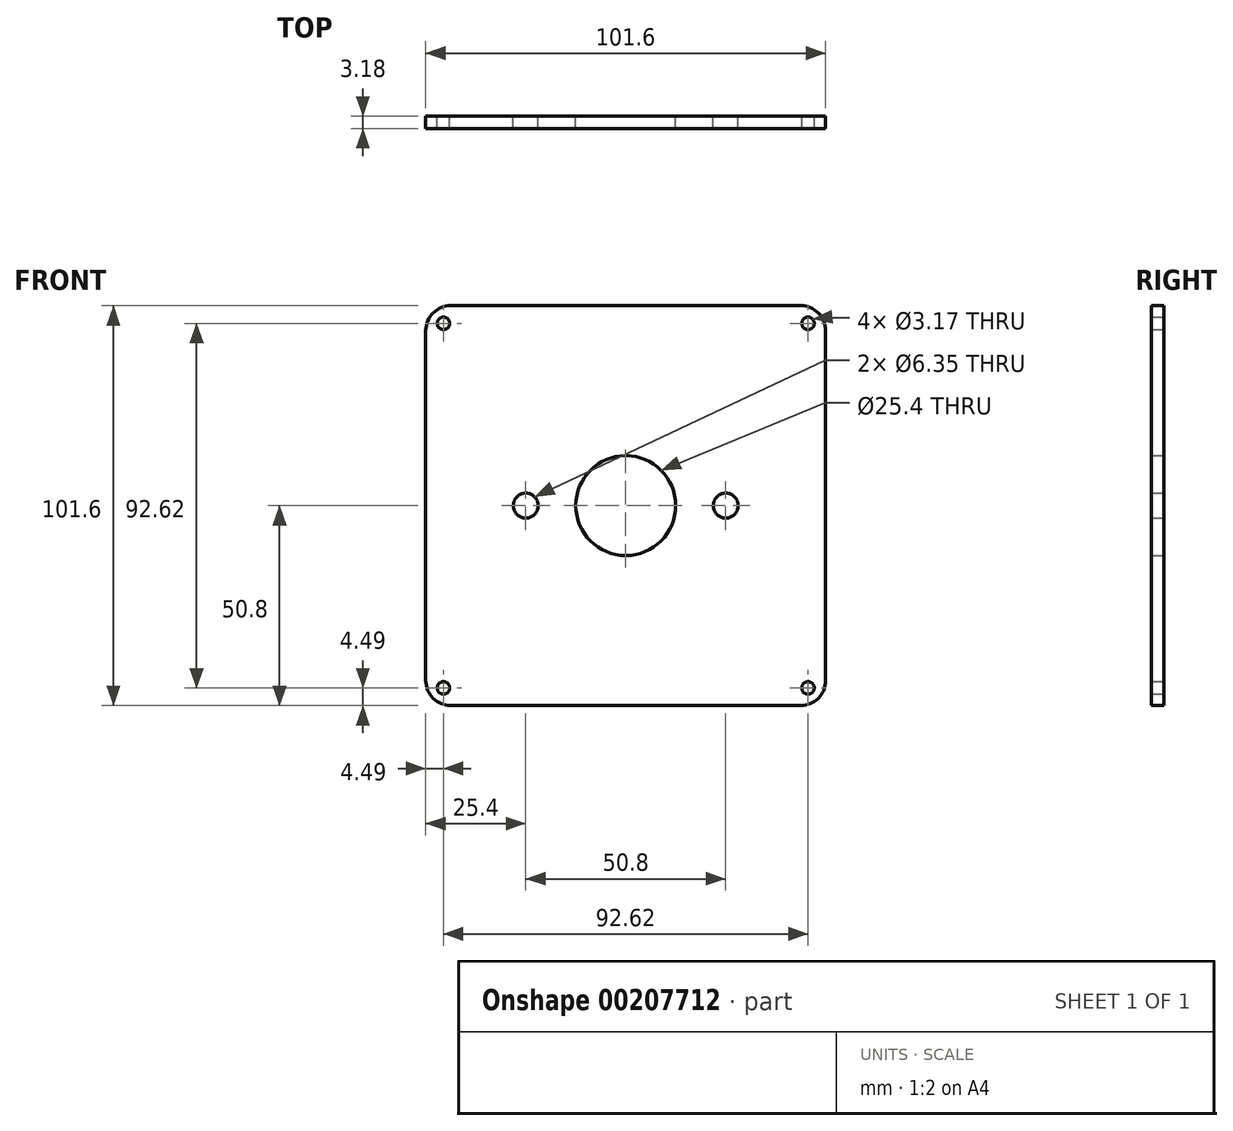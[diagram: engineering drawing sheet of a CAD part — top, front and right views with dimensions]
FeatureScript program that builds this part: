
annotation { "Feature Type Name" : "Feature", "Feature Type Description" : "" }
export const myFeature = defineFeature(function(context is Context, id is Id, definition is map)
    precondition{}
    {
        {
            var Q0;
            Q0=qCreatedBy(makeId("Front.planeOp"),FACE);
            var sketch = newSketch(context, id + "F0", { "sketchPlane" : qUnion([Q0])});
            skLineSegment(sketch, "E0.bottom", {"start": v(44.45, -50.8) * mm, "end": v(-44.45, -50.8) * mm});
            skLineSegment(sketch, "E0.top", {"start": v(44.45, 50.8) * mm, "end": v(-44.45, 50.8) * mm});
            skLineSegment(sketch, "E0.left", {"start": v(50.8, -44.45) * mm, "end": v(50.8, 44.45) * mm});
            skLineSegment(sketch, "E0.right", {"start": v(-50.8, -44.45) * mm, "end": v(-50.8, 44.45) * mm});
            skPoint(sketch, "E0.middle", {"position": v(0, 0) * mm});
            skCircle(sketch, "E1", {"center": v(0, 0) * mm, "radius": 12.7 * mm});
            skCircle(sketch, "E2", {"center": v(-25.4, 0) * mm, "radius": 3.18 * mm});
            skCircle(sketch, "E3", {"center": v(25.4, 0) * mm, "radius": 3.18 * mm});
            skCircle(sketch, "E4", {"center": v(0, 0) * mm, "radius": 25.4 * mm, "construction": true});
            skPoint(sketch, "E5.visualSharp", {"position": v(-50.8, 50.8) * mm});
            skArc(sketch, "E5.filletArc", {"start": v(-44.45, 50.8) * mm, "mid": v(-48.94, 48.94) * mm, "end": v(-50.8, 44.45) * mm});
            skPoint(sketch, "E6.visualSharp", {"position": v(-50.8, -50.8) * mm});
            skArc(sketch, "E6.filletArc", {"start": v(-50.8, -44.45) * mm, "mid": v(-48.94, -48.94) * mm, "end": v(-44.45, -50.8) * mm});
            skPoint(sketch, "E7.visualSharp", {"position": v(50.8, -50.8) * mm});
            skArc(sketch, "E7.filletArc", {"start": v(44.45, -50.8) * mm, "mid": v(48.94, -48.94) * mm, "end": v(50.8, -44.45) * mm});
            skPoint(sketch, "E8.visualSharp", {"position": v(50.8, 50.8) * mm});
            skArc(sketch, "E8.filletArc", {"start": v(50.8, 44.45) * mm, "mid": v(48.94, 48.94) * mm, "end": v(44.45, 50.8) * mm});
            skLineSegment(sketch, "E9", {"start": v(0, 0) * mm, "end": v(-50.8, 50.8) * mm, "construction": true});
            skCircle(sketch, "E10", {"center": v(-46.3, 46.3) * mm, "radius": 1.59 * mm});
            skCircle(sketch, "E11.MirrorC", {"center": v(46.3, 46.3) * mm, "radius": 1.59 * mm});
            skCircle(sketch, "E12.MirrorC", {"center": v(-46.3, -46.3) * mm, "radius": 1.59 * mm});
            skCircle(sketch, "E13.MirrorC", {"center": v(46.3, -46.3) * mm, "radius": 1.59 * mm});
            skSolve(sketch);
        }
        {
            var Q0;
            Q0=makeQuery(id+"F0.imprint","IMPRINT",FACE,{"disambiguationData":[TD([[makeQuery(id+"F0.imprint","IMPRINT",EDGE,{"derivedFrom":sQuery(id+"F0.wireOp",EDGE,"E0.bottom")}),-1.0]])]});
            extrude(context, id + "F1", {"entities" : qUnion([Q0]), "depth" : 3.17 * mm});
        }
    });
